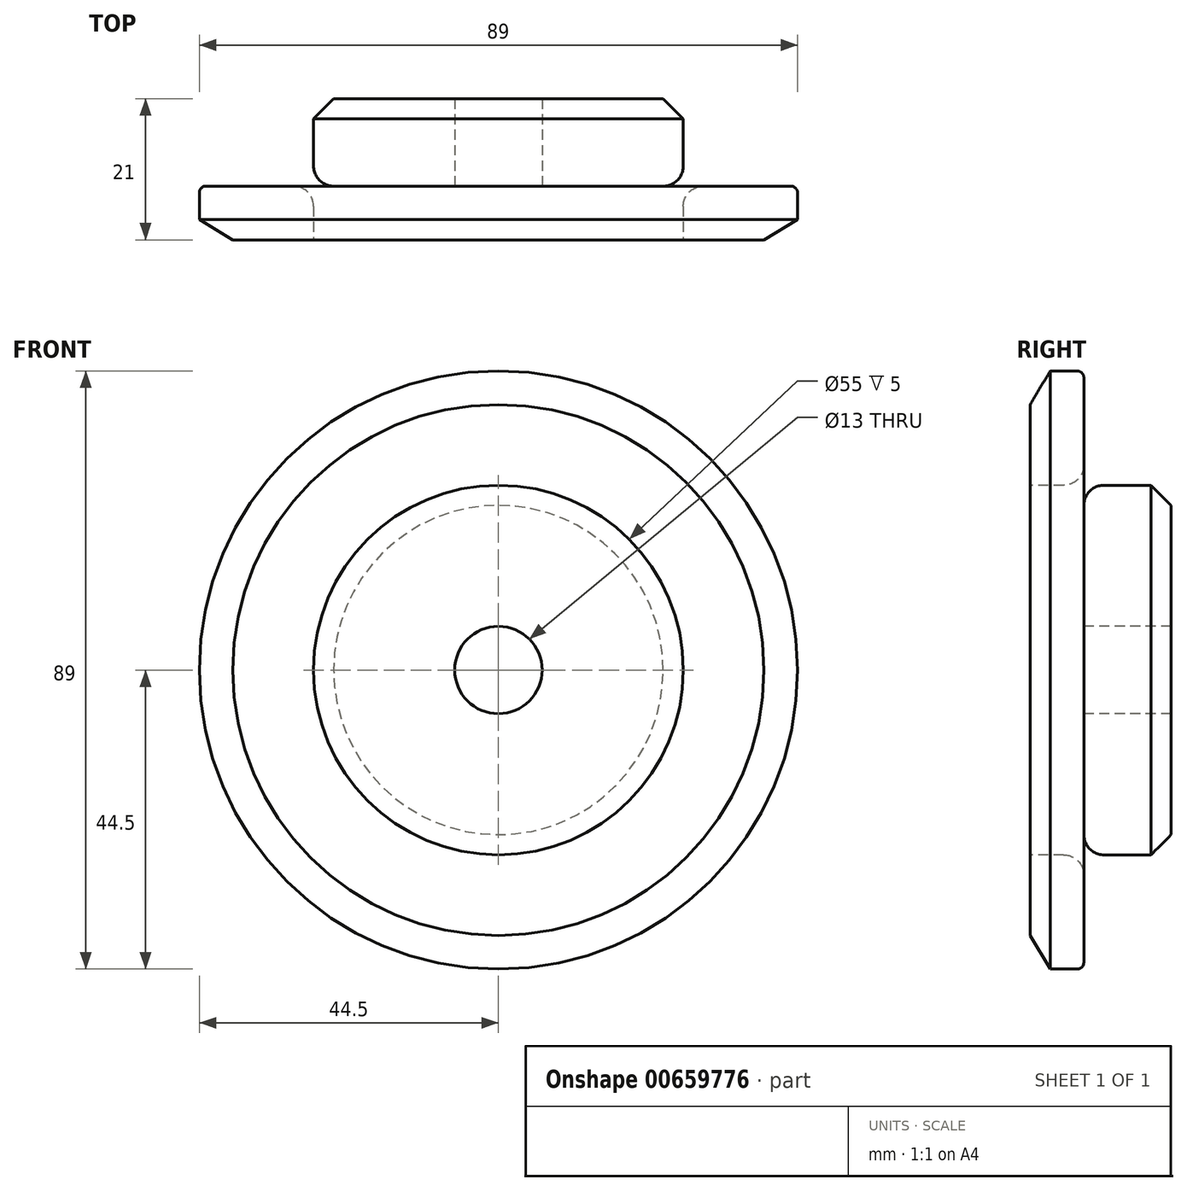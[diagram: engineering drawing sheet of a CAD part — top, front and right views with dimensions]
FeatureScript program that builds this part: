
annotation { "Feature Type Name" : "Feature", "Feature Type Description" : "" }
export const myFeature = defineFeature(function(context is Context, id is Id, definition is map)
    precondition{}
    {
        {
            var Q0;
            Q0=qCreatedBy(makeId("Right.planeOp"),FACE);
            var sketch = newSketch(context, id + "F0", { "sketchPlane" : qUnion([Q0])});
            skLineSegment(sketch, "E0", {"start": v(0, 0) * mm, "end": v(21, 0) * mm, "construction": true});
            skLineSegment(sketch, "E1.bottom", {"start": v(0, 44.5) * mm, "end": v(8, 44.5) * mm});
            skLineSegment(sketch, "E1.top", {"start": v(0, 6.5) * mm, "end": v(8, 6.5) * mm});
            skLineSegment(sketch, "E1.left", {"start": v(0, 44.5) * mm, "end": v(0, 6.5) * mm});
            skLineSegment(sketch, "E1.right", {"start": v(8, 44.5) * mm, "end": v(8, 6.5) * mm});
            skLineSegment(sketch, "E2.bottom", {"start": v(0, 6.5) * mm, "end": v(21, 6.5) * mm});
            skLineSegment(sketch, "E2.top", {"start": v(0, 27.5) * mm, "end": v(21, 27.5) * mm});
            skLineSegment(sketch, "E2.left", {"start": v(0, 6.5) * mm, "end": v(0, 27.5) * mm});
            skLineSegment(sketch, "E2.right", {"start": v(21, 6.5) * mm, "end": v(21, 27.5) * mm});
            skLineSegment(sketch, "E3.MirrorCS", {"start": v(0, -6.5) * mm, "end": v(8, -6.5) * mm});
            skLineSegment(sketch, "E4.MirrorCS", {"start": v(0, -27.5) * mm, "end": v(21, -27.5) * mm});
            skLineSegment(sketch, "E5.MirrorCS", {"start": v(0, -6.5) * mm, "end": v(21, -6.5) * mm});
            skLineSegment(sketch, "E6.MirrorCS", {"start": v(8, -44.5) * mm, "end": v(8, -6.5) * mm});
            skLineSegment(sketch, "E7.MirrorCS", {"start": v(0, -44.5) * mm, "end": v(0, -6.5) * mm});
            skLineSegment(sketch, "E8.MirrorCS", {"start": v(0, -6.5) * mm, "end": v(0, -27.5) * mm});
            skLineSegment(sketch, "E9.MirrorCS", {"start": v(0, -44.5) * mm, "end": v(8, -44.5) * mm});
            skLineSegment(sketch, "E10.MirrorCS", {"start": v(21, -6.5) * mm, "end": v(21, -27.5) * mm});
            skSolve(sketch);
        }
        {
            var Q0;
            {var subQ5=sQuery(id+"F0.wireOp",EDGE,"E2.right");Q0=makeQuery(id+"F0.imprint","IMPRINT",FACE,{"disambiguationData":[TD([[makeQuery(id+"F0.imprint","IMPRINT",EDGE,{"derivedFrom":subQ5}),1.0]])]});}
            var Q1;
            {var subQ5=sQuery(id+"F0.wireOp",EDGE,"E2.left");Q1=makeQuery(id+"F0.imprint","IMPRINT",FACE,{"disambiguationData":[TD([[makeQuery(id+"F0.imprint","IMPRINT",EDGE,{"derivedFrom":subQ5}),-1.0]])]});}
            var Q2;
            {var subQ0=sQuery(id+"F0.wireOp",EDGE,"E1.bottom");Q2=makeQuery(id+"F0.imprint","IMPRINT",FACE,{"disambiguationData":[TD([[makeQuery(id+"F0.imprint","IMPRINT",EDGE,{"derivedFrom":subQ0}),-1.0]])]});}
            var Q3;
            Q3=sQuery(id+"F0.wireOp",EDGE,"E0");
            revolve(context, id + "F1", {"entities" : qUnion([Q0, Q1, Q2]), "axis" : qUnion([Q3]), "revolveType" : RevolveType.FULL});
        }
        {
            var Q0;
            Q0=makeQuery(id+"F1.opRevolve","SWEPT_EDGE",EDGE,{"disambiguationData":[OSD([sQuery(id+"F0.wireOp",EDGE,"E1.right"),sQuery(id+"F0.wireOp",EDGE,"E2.top")])]});
            fillet(context, id + "F2", {"entities" : qUnion([Q0]), "radius" : 3 * mm, "tangentPropagation" : true, "allowEdgeOverflow" : false});
        }
        {
            var Q0;
            Q0=makeQuery(id+"F1.opRevolve","SWEPT_EDGE",EDGE,{"disambiguationData":[OSD([sQuery(id+"F0.wireOp",EDGE,"E1.bottom"),sQuery(id+"F0.wireOp",EDGE,"E1.right")])]});
            fillet(context, id + "F3", {"entities" : qUnion([Q0]), "radius" : 1 * mm, "tangentPropagation" : true, "allowEdgeOverflow" : false});
        }
        {
            var Q0;
            Q0=makeQuery(id+"F1.opRevolve","SWEPT_EDGE",EDGE,{"disambiguationData":[OSD([sQuery(id+"F0.wireOp",EDGE,"E2.top"),sQuery(id+"F0.wireOp",EDGE,"E2.right")])]});
            chamfer(context, id + "F4", {"entities" : qUnion([Q0]), "width" : 3 * mm, "tangentPropagation" : true});
        }
        {
            var Q0;
            Q0=makeQuery(id+"F1.opRevolve","SWEPT_EDGE",EDGE,{"disambiguationData":[OSD([sQuery(id+"F0.wireOp",EDGE,"E1.bottom"),sQuery(id+"F0.wireOp",EDGE,"E1.left")])]});
            chamfer(context, id + "F5", {"entities" : qUnion([Q0]), "chamferType" : ChamferType.TWO_OFFSETS, "width1" : 5 * mm, "oppositeDirection" : false, "width2" : 3 * mm, "tangentPropagation" : true});
        }
    });
